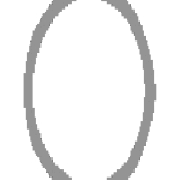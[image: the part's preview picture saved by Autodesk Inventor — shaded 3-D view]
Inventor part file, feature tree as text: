
AUTODESK INVENTOR PART (.ipt)
format: ipt  version: 2021 (Build 250183000, 183)  size: 110,080 bytes
history: native  units: in
note: dims shown in document units (in); Inventor stores cm internally (conversion verified against a paired STEP export)
features: other x4, sketch x3, plane x1
ambient origin geometry x8: Origin, YZ Plane, XZ Plane, XY Plane, X Axis, Y Axis, Z Axis, Center Point
bodies: Solid1 (feature_tree), Body (feature_tree)
feature tree (8):
  other  "Driven Length"
  other  "Frame Generator"
  other  "Start Plane"
  other  "End Plane"
  sketch  "Sketch"  dims[d2=11.6in d4=-0.0in d5=11.6in d6=0.12in d7=0.0in d10=90.0deg d9=11.6in]
  sketch  "Sketch4"  dims[d0=1.0in]
  plane  "Work Plane4"
  sketch  "Sketch5"  dims[d1=0.065in]
